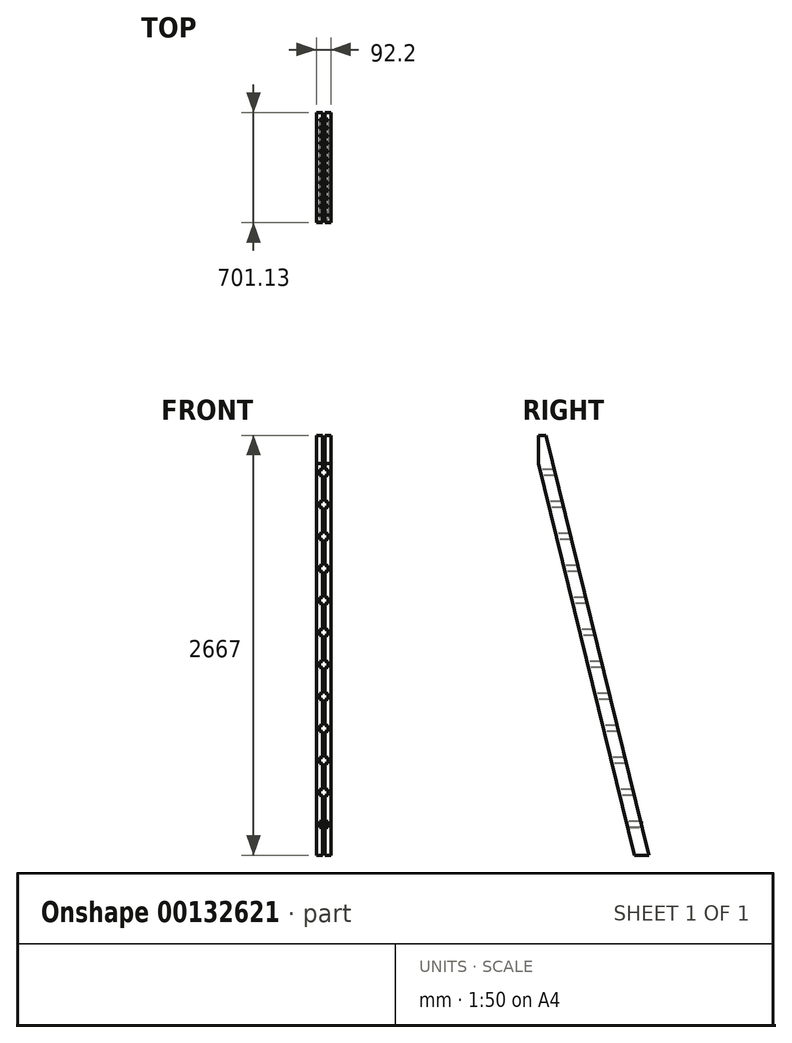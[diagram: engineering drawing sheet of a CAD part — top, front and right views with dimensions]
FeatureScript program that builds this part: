
annotation { "Feature Type Name" : "Feature", "Feature Type Description" : "" }
export const myFeature = defineFeature(function(context is Context, id is Id, definition is map)
    precondition{}
    {
        {
            var Q0;
            Q0=qCreatedBy(makeId("Right.planeOp"),FACE);
            var sketch = newSketch(context, id + "F0", { "sketchPlane" : qUnion([Q0])});
            skLineSegment(sketch, "E0", {"start": v(0, 0) * mm, "end": v(609.6, 0) * mm, "construction": true});
            skLineSegment(sketch, "E1", {"start": v(0, 0) * mm, "end": v(0, 2667) * mm, "construction": true});
            skLineSegment(sketch, "E2", {"start": v(0, 2667) * mm, "end": v(0, 2489.2) * mm});
            skLineSegment(sketch, "E3", {"start": v(0, 2489.2) * mm, "end": v(609.6, 0) * mm});
            skLineSegment(sketch, "E4.0", {"start": v(47.98, 2667) * mm, "end": v(701.13, 0) * mm});
            skLineSegment(sketch, "E5", {"start": v(0, 2667) * mm, "end": v(47.98, 2667) * mm});
            skLineSegment(sketch, "E6", {"start": v(609.6, 0) * mm, "end": v(701.13, 0) * mm});
            skSolve(sketch);
        }
        {
            var Q0;
            Q0=makeQuery(id+"F0.imprint","IMPRINT",FACE,{"disambiguationData":[TD([[makeQuery(id+"F0.imprint","IMPRINT",EDGE,{"derivedFrom":sQuery(id+"F0.wireOp",EDGE,"E2")}),1.0]])]});
            extrude(context, id + "F1", {"entities" : qUnion([Q0]), "depth" : 38.1 * mm});
        }
        {
            assignVariable(context, id + "F2", {"name" : "Width", "anyValue" : 16});
        }
        {
            var Q0;
            Q0=makeQuery(id+"F1.opExtrude","CAP_FACE",FACE,{"disambiguationData":[OSD([sQuery(id+"F0.wireOp",EDGE,"E2"),sQuery(id+"F0.wireOp",EDGE,"E3"),sQuery(id+"F0.wireOp",EDGE,"E4.0"),sQuery(id+"F0.wireOp",EDGE,"E5"),sQuery(id+"F0.wireOp",EDGE,"E6")])],"isStart":true});
            cPlane(context, id + "F3", {"entities" : qUnion([Q0]), "cplaneType" : CPlaneType.OFFSET, "offset" : (getVariable(context, 'Width') / 2) * mm, "width" : 152.4 * mm, "height" : 152.4 * mm});
        }
        {
            var Q0;
            Q0=qCreatedBy(id+"F3.planeOp",FACE);
            var sketch = newSketch(context, id + "F4", { "sketchPlane" : qUnion([Q0])});
            skLineSegment(sketch, "E7.0.0", {"start": v(0, 2667) * mm, "end": v(-47.98, 2667) * mm, "construction": true});
            skLineSegment(sketch, "E7.0.1", {"start": v(-47.98, 2667) * mm, "end": v(-701.13, 0) * mm, "construction": true});
            skLineSegment(sketch, "E7.0.2", {"start": v(-701.13, 0) * mm, "end": v(-609.6, 0) * mm, "construction": true});
            skLineSegment(sketch, "E7.0.3", {"start": v(-609.6, 0) * mm, "end": v(0, 2489.2) * mm, "construction": true});
            skLineSegment(sketch, "E7.0.4", {"start": v(0, 2489.2) * mm, "end": v(0, 2667) * mm, "construction": true});
            skLineSegment(sketch, "E8", {"start": v(-651.6, 215.9) * mm, "end": v(-562.7, 215.9) * mm});
            skLineSegment(sketch, "E9", {"start": v(-562.7, 215.9) * mm, "end": v(-562.7, 177.8) * mm});
            skLineSegment(sketch, "E10", {"start": v(-562.7, 177.8) * mm, "end": v(-651.6, 177.8) * mm});
            skLineSegment(sketch, "E11", {"start": v(-651.6, 177.8) * mm, "end": v(-651.6, 215.9) * mm});
            skLineSegment(sketch, "E12", {"start": v(-655.36, 0) * mm, "end": v(-2.22, 2667) * mm, "construction": true});
            skLineSegment(sketch, "E13", {"start": v(-651.6, 177.8) * mm, "end": v(-562.7, 215.9) * mm, "construction": true});
            skLineSegment(sketch, "E14", {"start": v(-562.7, 177.8) * mm, "end": v(-651.6, 215.9) * mm, "construction": true});
            skLineSegment(sketch, "E15", {"start": v(-607.16, 215.9) * mm, "end": v(-607.16, 196.85) * mm, "construction": true});
            skSolve(sketch);
        }
        {
            var Q0;
            Q0=makeQuery(id+"F4.imprint","IMPRINT",FACE,{"disambiguationData":[TD([[makeQuery(id+"F4.imprint","IMPRINT",EDGE,{"derivedFrom":sQuery(id+"F4.wireOp",EDGE,"E8")}),-1.0]])]});
            extrude(context, id + "F5", {"entities" : qUnion([Q0]), "depth" : ((getVariable(context, 'Width') / 2) + 0.75) * mm, "hasSecondDirection" : true, "secondDirectionOppositeDirection" : true, "secondDirectionDepth" : ((getVariable(context, 'Width') / 2) + 0.75) * mm});
        }
        {
            var Q0;
            Q0=makeQuery(id+"F1.opExtrude","CAP_FACE",FACE,{"disambiguationData":[OSD([sQuery(id+"F0.wireOp",EDGE,"E2"),sQuery(id+"F0.wireOp",EDGE,"E3"),sQuery(id+"F0.wireOp",EDGE,"E4.0"),sQuery(id+"F0.wireOp",EDGE,"E5"),sQuery(id+"F0.wireOp",EDGE,"E6")])],"isStart":true});
            var sketch = newSketch(context, id + "F6", { "sketchPlane" : qUnion([Q0])});
            skLineSegment(sketch, "E16.0.0", {"start": v(0, 2667) * mm, "end": v(-47.98, 2667) * mm, "construction": true});
            skLineSegment(sketch, "E16.0.1", {"start": v(-47.98, 2667) * mm, "end": v(-701.13, 0) * mm, "construction": true});
            skLineSegment(sketch, "E16.0.2", {"start": v(-701.13, 0) * mm, "end": v(-609.6, 0) * mm, "construction": true});
            skLineSegment(sketch, "E16.0.3", {"start": v(-609.6, 0) * mm, "end": v(0, 2489.2) * mm, "construction": true});
            skLineSegment(sketch, "E16.0.4", {"start": v(0, 2489.2) * mm, "end": v(0, 2667) * mm, "construction": true});
            skLineSegment(sketch, "E17", {"start": v(-701.13, 0) * mm, "end": v(-701.13, 2667) * mm});
            skLineSegment(sketch, "E18", {"start": v(0, 2489.2) * mm, "end": v(0, 0) * mm});
            skLineSegment(sketch, "E19.0", {"start": v(-651.6, 215.9) * mm, "end": v(-562.7, 215.9) * mm, "construction": true});
            skLineSegment(sketch, "E20.0", {"start": v(-562.7, 177.8) * mm, "end": v(-651.6, 177.8) * mm, "construction": true});
            skLineSegment(sketch, "E21", {"start": v(-701.13, 215.9) * mm, "end": v(0, 215.9) * mm});
            skLineSegment(sketch, "E22", {"start": v(-701.13, 177.8) * mm, "end": v(0, 177.8) * mm});
            skLineSegment(sketch, "E23.0.1.0", {"start": v(-701.13, 419.1) * mm, "end": v(0, 419.1) * mm});
            skLineSegment(sketch, "E23.0.1.1", {"start": v(-701.13, 381) * mm, "end": v(0, 381) * mm});
            skLineSegment(sketch, "E23.0.2.0", {"start": v(-701.13, 622.3) * mm, "end": v(0, 622.3) * mm});
            skLineSegment(sketch, "E23.0.2.1", {"start": v(-701.13, 584.2) * mm, "end": v(0, 584.2) * mm});
            skLineSegment(sketch, "E23.0.3.0", {"start": v(-701.13, 825.5) * mm, "end": v(0, 825.5) * mm});
            skLineSegment(sketch, "E23.0.3.1", {"start": v(-701.13, 787.4) * mm, "end": v(0, 787.4) * mm});
            skLineSegment(sketch, "E23.0.4.0", {"start": v(-701.13, 1028.7) * mm, "end": v(0, 1028.7) * mm});
            skLineSegment(sketch, "E23.0.4.1", {"start": v(-701.13, 990.6) * mm, "end": v(0, 990.6) * mm});
            skLineSegment(sketch, "E23.0.5.0", {"start": v(-701.13, 1231.9) * mm, "end": v(0, 1231.9) * mm});
            skLineSegment(sketch, "E23.0.5.1", {"start": v(-701.13, 1193.8) * mm, "end": v(0, 1193.8) * mm});
            skLineSegment(sketch, "E23.0.6.0", {"start": v(-701.13, 1435.1) * mm, "end": v(0, 1435.1) * mm});
            skLineSegment(sketch, "E23.0.6.1", {"start": v(-701.13, 1397) * mm, "end": v(0, 1397) * mm});
            skLineSegment(sketch, "E23.0.7.0", {"start": v(-701.13, 1638.3) * mm, "end": v(0, 1638.3) * mm});
            skLineSegment(sketch, "E23.0.7.1", {"start": v(-701.13, 1600.2) * mm, "end": v(0, 1600.2) * mm});
            skLineSegment(sketch, "E23.0.8.0", {"start": v(-701.13, 1841.5) * mm, "end": v(0, 1841.5) * mm});
            skLineSegment(sketch, "E23.0.8.1", {"start": v(-701.13, 1803.4) * mm, "end": v(0, 1803.4) * mm});
            skLineSegment(sketch, "E23.0.9.0", {"start": v(-701.13, 2044.7) * mm, "end": v(0, 2044.7) * mm});
            skLineSegment(sketch, "E23.0.9.1", {"start": v(-701.13, 2006.6) * mm, "end": v(0, 2006.6) * mm});
            skLineSegment(sketch, "E23.0.10.0", {"start": v(-701.13, 2247.9) * mm, "end": v(0, 2247.9) * mm});
            skLineSegment(sketch, "E23.0.10.1", {"start": v(-701.13, 2209.8) * mm, "end": v(0, 2209.8) * mm});
            skLineSegment(sketch, "E23.0.11.0", {"start": v(-701.13, 2451.1) * mm, "end": v(0, 2451.1) * mm});
            skLineSegment(sketch, "E23.0.11.1", {"start": v(-701.13, 2413) * mm, "end": v(0, 2413) * mm});
            skLineSegment(sketch, "E23.direction1", {"start": v(-701.13, 177.8) * mm, "end": v(-677.13, 177.8) * mm, "construction": true});
            skLineSegment(sketch, "E23.direction2", {"start": v(-701.13, 177.8) * mm, "end": v(-701.13, 381) * mm, "construction": true});
            skSolve(sketch);
        }
        {
            var Q0;
            {var subQ0=sQuery(id+"F6.wireOp",EDGE,"E21");var subQ1=makeQuery(id+"F1.opExtrude","CAP_EDGE",EDGE,{"disambiguationData":[OSD([sQuery(id+"F0.wireOp",EDGE,"E4.0")])],"isStart":true});var subQ2=makeQuery(id+"F6.imprint","INTERSECT",VERTEX,{"derivedFrom":[subQ1,subQ0]});Q0=makeQuery(id+"F6.imprint","IMPRINT",FACE,{"disambiguationData":[TD([[makeQuery(id+"F6.imprint","IMPRINT",EDGE,{"disambiguationData":[TD([[subQ2,-1.0]])],"derivedFrom":subQ0}),-1.0]])]});}
            var Q1;
            {var subQ0=sQuery(id+"F6.wireOp",EDGE,"E23.0.1.0");var subQ1=makeQuery(id+"F1.opExtrude","CAP_EDGE",EDGE,{"disambiguationData":[OSD([sQuery(id+"F0.wireOp",EDGE,"E4.0")])],"isStart":true});var subQ2=makeQuery(id+"F6.imprint","INTERSECT",VERTEX,{"derivedFrom":[subQ1,subQ0]});Q1=makeQuery(id+"F6.imprint","IMPRINT",FACE,{"disambiguationData":[TD([[makeQuery(id+"F6.imprint","IMPRINT",EDGE,{"disambiguationData":[TD([[subQ2,-1.0]])],"derivedFrom":subQ0}),-1.0]])]});}
            var Q2;
            {var subQ0=sQuery(id+"F6.wireOp",EDGE,"E23.0.2.0");var subQ1=makeQuery(id+"F1.opExtrude","CAP_EDGE",EDGE,{"disambiguationData":[OSD([sQuery(id+"F0.wireOp",EDGE,"E4.0")])],"isStart":true});var subQ2=makeQuery(id+"F6.imprint","INTERSECT",VERTEX,{"derivedFrom":[subQ1,subQ0]});Q2=makeQuery(id+"F6.imprint","IMPRINT",FACE,{"disambiguationData":[TD([[makeQuery(id+"F6.imprint","IMPRINT",EDGE,{"disambiguationData":[TD([[subQ2,-1.0]])],"derivedFrom":subQ0}),-1.0]])]});}
            var Q3;
            {var subQ0=sQuery(id+"F6.wireOp",EDGE,"E23.0.3.0");var subQ1=makeQuery(id+"F1.opExtrude","CAP_EDGE",EDGE,{"disambiguationData":[OSD([sQuery(id+"F0.wireOp",EDGE,"E4.0")])],"isStart":true});var subQ2=makeQuery(id+"F6.imprint","INTERSECT",VERTEX,{"derivedFrom":[subQ1,subQ0]});Q3=makeQuery(id+"F6.imprint","IMPRINT",FACE,{"disambiguationData":[TD([[makeQuery(id+"F6.imprint","IMPRINT",EDGE,{"disambiguationData":[TD([[subQ2,-1.0]])],"derivedFrom":subQ0}),-1.0]])]});}
            var Q4;
            {var subQ0=sQuery(id+"F6.wireOp",EDGE,"E23.0.4.0");var subQ1=makeQuery(id+"F1.opExtrude","CAP_EDGE",EDGE,{"disambiguationData":[OSD([sQuery(id+"F0.wireOp",EDGE,"E4.0")])],"isStart":true});var subQ2=makeQuery(id+"F6.imprint","INTERSECT",VERTEX,{"derivedFrom":[subQ1,subQ0]});Q4=makeQuery(id+"F6.imprint","IMPRINT",FACE,{"disambiguationData":[TD([[makeQuery(id+"F6.imprint","IMPRINT",EDGE,{"disambiguationData":[TD([[subQ2,-1.0]])],"derivedFrom":subQ0}),-1.0]])]});}
            var Q5;
            {var subQ0=sQuery(id+"F6.wireOp",EDGE,"E23.0.5.0");var subQ1=makeQuery(id+"F1.opExtrude","CAP_EDGE",EDGE,{"disambiguationData":[OSD([sQuery(id+"F0.wireOp",EDGE,"E4.0")])],"isStart":true});var subQ2=makeQuery(id+"F6.imprint","INTERSECT",VERTEX,{"derivedFrom":[subQ1,subQ0]});Q5=makeQuery(id+"F6.imprint","IMPRINT",FACE,{"disambiguationData":[TD([[makeQuery(id+"F6.imprint","IMPRINT",EDGE,{"disambiguationData":[TD([[subQ2,-1.0]])],"derivedFrom":subQ0}),-1.0]])]});}
            var Q6;
            {var subQ0=sQuery(id+"F6.wireOp",EDGE,"E23.0.6.0");var subQ1=makeQuery(id+"F1.opExtrude","CAP_EDGE",EDGE,{"disambiguationData":[OSD([sQuery(id+"F0.wireOp",EDGE,"E4.0")])],"isStart":true});var subQ2=makeQuery(id+"F6.imprint","INTERSECT",VERTEX,{"derivedFrom":[subQ1,subQ0]});Q6=makeQuery(id+"F6.imprint","IMPRINT",FACE,{"disambiguationData":[TD([[makeQuery(id+"F6.imprint","IMPRINT",EDGE,{"disambiguationData":[TD([[subQ2,-1.0]])],"derivedFrom":subQ0}),-1.0]])]});}
            var Q7;
            {var subQ0=sQuery(id+"F6.wireOp",EDGE,"E23.0.7.0");var subQ1=makeQuery(id+"F1.opExtrude","CAP_EDGE",EDGE,{"disambiguationData":[OSD([sQuery(id+"F0.wireOp",EDGE,"E4.0")])],"isStart":true});var subQ2=makeQuery(id+"F6.imprint","INTERSECT",VERTEX,{"derivedFrom":[subQ1,subQ0]});Q7=makeQuery(id+"F6.imprint","IMPRINT",FACE,{"disambiguationData":[TD([[makeQuery(id+"F6.imprint","IMPRINT",EDGE,{"disambiguationData":[TD([[subQ2,-1.0]])],"derivedFrom":subQ0}),-1.0]])]});}
            var Q8;
            {var subQ0=sQuery(id+"F6.wireOp",EDGE,"E23.0.8.0");var subQ1=makeQuery(id+"F1.opExtrude","CAP_EDGE",EDGE,{"disambiguationData":[OSD([sQuery(id+"F0.wireOp",EDGE,"E4.0")])],"isStart":true});var subQ2=makeQuery(id+"F6.imprint","INTERSECT",VERTEX,{"derivedFrom":[subQ1,subQ0]});Q8=makeQuery(id+"F6.imprint","IMPRINT",FACE,{"disambiguationData":[TD([[makeQuery(id+"F6.imprint","IMPRINT",EDGE,{"disambiguationData":[TD([[subQ2,-1.0]])],"derivedFrom":subQ0}),-1.0]])]});}
            var Q9;
            {var subQ0=sQuery(id+"F6.wireOp",EDGE,"E23.0.9.0");var subQ1=makeQuery(id+"F1.opExtrude","CAP_EDGE",EDGE,{"disambiguationData":[OSD([sQuery(id+"F0.wireOp",EDGE,"E4.0")])],"isStart":true});var subQ2=makeQuery(id+"F6.imprint","INTERSECT",VERTEX,{"derivedFrom":[subQ1,subQ0]});Q9=makeQuery(id+"F6.imprint","IMPRINT",FACE,{"disambiguationData":[TD([[makeQuery(id+"F6.imprint","IMPRINT",EDGE,{"disambiguationData":[TD([[subQ2,-1.0]])],"derivedFrom":subQ0}),-1.0]])]});}
            var Q10;
            {var subQ0=sQuery(id+"F6.wireOp",EDGE,"E23.0.10.0");var subQ1=makeQuery(id+"F1.opExtrude","CAP_EDGE",EDGE,{"disambiguationData":[OSD([sQuery(id+"F0.wireOp",EDGE,"E4.0")])],"isStart":true});var subQ2=makeQuery(id+"F6.imprint","INTERSECT",VERTEX,{"derivedFrom":[subQ1,subQ0]});Q10=makeQuery(id+"F6.imprint","IMPRINT",FACE,{"disambiguationData":[TD([[makeQuery(id+"F6.imprint","IMPRINT",EDGE,{"disambiguationData":[TD([[subQ2,-1.0]])],"derivedFrom":subQ0}),-1.0]])]});}
            var Q11;
            {var subQ0=sQuery(id+"F6.wireOp",EDGE,"E23.0.11.0");var subQ1=makeQuery(id+"F1.opExtrude","CAP_EDGE",EDGE,{"disambiguationData":[OSD([sQuery(id+"F0.wireOp",EDGE,"E4.0")])],"isStart":true});var subQ2=makeQuery(id+"F6.imprint","INTERSECT",VERTEX,{"derivedFrom":[subQ1,subQ0]});Q11=makeQuery(id+"F6.imprint","IMPRINT",FACE,{"disambiguationData":[TD([[makeQuery(id+"F6.imprint","IMPRINT",EDGE,{"disambiguationData":[TD([[subQ2,-1.0]])],"derivedFrom":subQ0}),-1.0]])]});}
            extrude(context, id + "F7", {"entities" : qUnion([Q0, Q1, Q2, Q3, Q4, Q5, Q6, Q7, Q8, Q9, Q10, Q11]), "operationType" : NewBodyOperationType.REMOVE, "oppositeDirection" : true, "depth" : 19.05 * mm});
        }
        {
            var Q0;
            Q0=makeQuery(id+"F1.opExtrude","SWEPT_BODY",BODY,{"disambiguationData":[OSD([sQuery(id+"F0.wireOp",EDGE,"E2"),sQuery(id+"F0.wireOp",EDGE,"E3"),sQuery(id+"F0.wireOp",EDGE,"E4.0"),sQuery(id+"F0.wireOp",EDGE,"E5"),sQuery(id+"F0.wireOp",EDGE,"E6")])]});
            var Q1;
            Q1=qCreatedBy(id+"F3.planeOp",FACE);
            mirror(context, id + "F8", {"entities" : qUnion([Q0]), "mirrorPlane" : qUnion([Q1])});
        }
    });
